FCSTD DOCUMENT  (FreeCAD 0.16R6704 (Git))
Label: Proxxon IBS-E
License: All rights reserved
LicenseURL: http://en.wikipedia.org/wiki/All_rights_reserved
objects: Sketcher::SketchObject×10, Drawing::FeatureViewPython×10, PartDesign::Pocket×9, Drawing::FeatureViewPart×3, Drawing::FeaturePage×2, PartDesign::Fillet×2, Mesh::Feature×1, PartDesign::Pad×1, PartDesign::Chamfer×1
note: 33 computed .brp shape members not serialized (recipe doc carries the construction recipe); baked Part::Feature solids carry a one-line shape summary decoded from their .brp

FEATURE [Mesh::Feature] Proxxon_IBS_E  label="Proxxon_IBS-E"
  Placement = pos=(-33.5,-33.5,0) rot=(0,0,1;0rad)
FEATURE [Sketcher::SketchObject] Sketch
  sketch-geometry (22):
    g0: LineSegment [constr] StartX=-23 StartY=-23.75 StartZ=0 EndX=23 EndY=-23.75 EndZ=0
    g1: LineSegment [constr] StartX=23 StartY=-23.75 StartZ=0 EndX=23 EndY=23.75 EndZ=0
    g2: LineSegment StartX=23 StartY=23.75 StartZ=0 EndX=-23 EndY=23.75 EndZ=0
    g3: LineSegment [constr] StartX=-23 StartY=23.75 StartZ=0 EndX=-23 EndY=-23.75 EndZ=0
    g4: LineSegment StartX=-1 StartY=-23.75 StartZ=0 EndX=-1 EndY=-50.75 EndZ=0
    g5: LineSegment StartX=-1 StartY=-50.75 StartZ=0 EndX=-13 EndY=-50.75 EndZ=0
    g6: LineSegment StartX=-13 StartY=-50.75 StartZ=0 EndX=-13 EndY=-33.75 EndZ=0
    g7: LineSegment StartX=-13 StartY=-33.75 StartZ=0 EndX=-38 EndY=-33.75 EndZ=0
    g8: LineSegment StartX=-38 StartY=-33.75 StartZ=0 EndX=-38 EndY=27.75 EndZ=0
    g9: LineSegment StartX=-38 StartY=27.75 StartZ=0 EndX=38 EndY=27.75 EndZ=0
    g10: LineSegment StartX=38 StartY=27.75 StartZ=0 EndX=38 EndY=-33.75 EndZ=0
    g11: LineSegment StartX=38 StartY=-33.75 StartZ=0 EndX=13 EndY=-33.75 EndZ=0
    g12: LineSegment StartX=13 StartY=-33.75 StartZ=0 EndX=13 EndY=-50.75 EndZ=0
    g13: LineSegment StartX=13 StartY=-50.75 StartZ=0 EndX=1 EndY=-50.75 EndZ=0
    g14: LineSegment StartX=1 StartY=-50.75 StartZ=0 EndX=1 EndY=-23.75 EndZ=0
    g15: LineSegment StartX=-23 StartY=-15.2647 StartZ=0 EndX=-14.5147 EndY=-23.75 EndZ=0
    g16: LineSegment StartX=14.5147 StartY=-23.75 StartZ=0 EndX=23 EndY=-15.2647 EndZ=0
    g17: LineSegment StartX=-14.5147 StartY=-23.75 StartZ=0 EndX=-1 EndY=-23.75 EndZ=0
    g18: LineSegment StartX=1 StartY=-23.75 StartZ=0 EndX=14.5147 EndY=-23.75 EndZ=0
    g19: LineSegment StartX=-23 StartY=23.75 StartZ=0 EndX=-23 EndY=-15.2647 EndZ=0
    g20: LineSegment StartX=23 StartY=23.75 StartZ=0 EndX=23 EndY=-15.2647 EndZ=0
    g21: LineSegment [constr] StartX=-23 StartY=-23.75 StartZ=0 EndX=-18.7574 EndY=-19.5074 EndZ=0
  constraints (65):
    c: Coincident(g0,g1)
    c: Coincident(g1,g2)
    c: Coincident(g2,g3)
    c: Coincident(g3,g0)
    c: Horizontal(g0)
    c: Horizontal(g2)
    c: Vertical(g1)
    c: Vertical(g3)
    c: DistanceY(g3,g3) = 47.5
    c: DistanceX(g2,g2) = 46
    c: Vertical(g4)
    c: Coincident(g4,g5)
    c: Horizontal(g5)
    c: Coincident(g5,g6)
    c: Vertical(g6)
    c: Coincident(g6,g7)
    c: Horizontal(g7)
    c: Coincident(g7,g8)
    c: Vertical(g8)
    c: Coincident(g8,g9)
    c: Horizontal(g9)
    c: Coincident(g9,g10)
    c: Vertical(g10)
    c: Coincident(g10,g11)
    c: Horizontal(g11)
    c: Coincident(g11,g12)
    c: Vertical(g12)
    c: Coincident(g12,g13)
    c: Horizontal(g13)
    c: Coincident(g13,g14)
    c: Vertical(g14)
    c: PointOnObject(g4,g13)
    c: Equal(g13,g5)
    c: Equal(g7,g11)
    c: PointOnObject(g6,g11)
    c: Symmetric(g8,g9,g-2)
    c: DistanceY(g1,g9) = 4
    c: DistanceY(g6,g0) = 10
    c: DistanceX(g5,g5) = 12
    c: DistanceX(g4,g13) = 2
    c: DistanceY(g6,g6) = 17
    c: Symmetric(g2,g1,g-2)
    c: Symmetric(g1,g0,g-1)
    c: DistanceX(g9,g9) = 76
    c: PointOnObject(g15,g3)
    c: PointOnObject(g15,g0)
    c: PointOnObject(g16,g0)
    c: PointOnObject(g16,g1)
    c: Angle(g3,g15) = 0.785398
    c: Angle(g16,g1) = 0.785398
    c: Equal(g15,g16)
    c: Coincident(g15,g17)
    c: Coincident(g4,g17)
    c: Coincident(g14,g18)
    c: Coincident(g16,g18)
    c: Coincident(g15,g19)
    c: Coincident(g2,g19)
    c: Coincident(g1,g20)
    c: Coincident(g16,g20)
    c: Coincident(g21,g0)
    c: PointOnObject(g21,g15)
    c: Distance(g21) = 6
    c: Perpendicular(g15,g21)
    c: PointOnObject(g4,g0)
    c: PointOnObject(g14,g0)
FEATURE [PartDesign::Pad] Pad
  Length = 20
  Length2 = 100
  Sketch = -> Sketch
  Type = 0
FEATURE [Sketcher::SketchObject] Sketch001
  ExternalGeometry = -> [Pad]
  Placement = pos=(-13,0,0) rot=(0.57735,-0.57735,-0.57735;2.0944rad)
  Support = -> Pad [Face7]
  sketch-geometry (3):
    g0: LineSegment [constr] StartX=33.75 StartY=10 StartZ=0 EndX=42.25 EndY=10 EndZ=0
    g1: LineSegment [constr] StartX=42.25 StartY=10 StartZ=0 EndX=50.75 EndY=10 EndZ=0
    g2: Circle CenterX=42.25 CenterY=10 CenterZ=0 NormalX=0 NormalY=0 NormalZ=1 Radius=2.2
  constraints (9):
    c: PointOnObject(g0,g-3)
    c: Horizontal(g0)
    c: Coincident(g0,g1)
    c: PointOnObject(g1,g-4)
    c: Horizontal(g1)
    c: Equal(g0,g1)
    c: Symmetric(g-3,g-3,g0)
    c: Coincident(g2,g0)
    c: Radius(g2) = 2.2
FEATURE [PartDesign::Pocket] Pocket
  Length = 5
  Sketch = -> Sketch001
  Type = 1
FEATURE [Sketcher::SketchObject] Sketch002
  ExternalGeometry = -> [Pocket]
  Placement = pos=(13,0,0) rot=(0.57735,0.57735,0.57735;2.0944rad)
  Support = -> Pocket [Face17]
  sketch-geometry (7):
    g0: LineSegment StartX=-40.2148 StartY=6.475 StartZ=0 EndX=-38.1797 EndY=10 EndZ=0
    g1: LineSegment StartX=-38.1797 StartY=10 StartZ=0 EndX=-40.2148 EndY=13.525 EndZ=0
    g2: LineSegment StartX=-40.2148 StartY=13.525 StartZ=0 EndX=-44.2852 EndY=13.525 EndZ=0
    g3: LineSegment StartX=-44.2852 StartY=13.525 StartZ=0 EndX=-46.3203 EndY=10 EndZ=0
    g4: LineSegment StartX=-46.3203 StartY=10 StartZ=0 EndX=-44.2852 EndY=6.475 EndZ=0
    g5: LineSegment StartX=-44.2852 StartY=6.475 StartZ=0 EndX=-40.2148 EndY=6.475 EndZ=0
    g6: Circle [constr] CenterX=-42.25 CenterY=10 CenterZ=0 NormalX=0 NormalY=0 NormalZ=1 Radius=4.07032
  constraints (16):
    c: Coincident(g0,g1)
    c: Coincident(g1,g2)
    c: Coincident(g2,g3)
    c: Coincident(g3,g4)
    c: Coincident(g4,g5)
    c: Coincident(g5,g0)
    c: Equal(g0, g1-g5) x5
    c: PointOnObject(g0,g6)
    c: PointOnObject(g1,g6)
    c: PointOnObject(g2,g6)
    c: PointOnObject(g3,g6)
    c: PointOnObject(g4,g6)
    c: PointOnObject(g5,g6)
    c: Coincident(g6,g-3)
    c: Distance(g2,g4) = 7.05
    c: Horizontal(g5)
FEATURE [PartDesign::Pocket] Pocket001
  Length = 4
  Sketch = -> Sketch002
  Type = 0
FEATURE [Sketcher::SketchObject] Sketch003
  ExternalGeometry = -> [Pocket001]
  Placement = pos=(0,27.75,0) rot=(0,0.707107,0.707107;3.14159rad)
  Support = -> Pocket001 [Face14]
  sketch-geometry (3):
    g0: LineSegment [constr] StartX=-30 StartY=10 StartZ=0 EndX=30 EndY=10 EndZ=0
    g1: Circle CenterX=-30 CenterY=10 CenterZ=0 NormalX=0 NormalY=0 NormalZ=1 Radius=2.2
    g2: Circle CenterX=30 CenterY=10 CenterZ=0 NormalX=0 NormalY=0 NormalZ=1 Radius=2.2
  constraints (5):
    c: Symmetric(g0,g0,g-2)
    c: Coincident(g1,g0)
    c: Coincident(g2,g0)
    c: Radius(g1) = 2.2
    c: Equal(g1,g2)
FEATURE [PartDesign::Pocket] Pocket002
  Length = 5
  Sketch = -> Sketch003
  Type = 1
FEATURE [Sketcher::SketchObject] Sketch004
  ExternalGeometry = -> [Pocket002]
  Placement = pos=(0,-33.75,0) rot=(1,0,0;1.5708rad)
  Support = -> Pocket002 [Face12]
  sketch-geometry (15):
    g0: LineSegment [constr] StartX=-30 StartY=10 StartZ=0 EndX=30 EndY=10 EndZ=0
    g1: LineSegment StartX=-33.525 StartY=7.96484 StartZ=0 EndX=-30 EndY=5.92968 EndZ=0
    g2: LineSegment StartX=-30 StartY=5.92968 StartZ=0 EndX=-26.475 EndY=7.96484 EndZ=0
    g3: LineSegment StartX=-26.475 StartY=7.96484 StartZ=0 EndX=-26.475 EndY=12.0352 EndZ=0
    g4: LineSegment StartX=-26.475 StartY=12.0352 StartZ=0 EndX=-30 EndY=14.0703 EndZ=0
    g5: LineSegment StartX=-30 StartY=14.0703 StartZ=0 EndX=-33.525 EndY=12.0352 EndZ=0
    g6: LineSegment StartX=-33.525 StartY=12.0352 StartZ=0 EndX=-33.525 EndY=7.96484 EndZ=0
    g7: Circle [constr] CenterX=-30 CenterY=10 CenterZ=0 NormalX=0 NormalY=0 NormalZ=1 Radius=4.07032
    g8: LineSegment StartX=33.525 StartY=7.96484 StartZ=0 EndX=33.525 EndY=12.0352 EndZ=0
    g9: LineSegment StartX=33.525 StartY=12.0352 StartZ=0 EndX=30 EndY=14.0703 EndZ=0
    g10: LineSegment StartX=30 StartY=14.0703 StartZ=0 EndX=26.475 EndY=12.0352 EndZ=0
    g11: LineSegment StartX=26.475 StartY=12.0352 StartZ=0 EndX=26.475 EndY=7.96484 EndZ=0
    g12: LineSegment StartX=26.475 StartY=7.96484 StartZ=0 EndX=30 EndY=5.92968 EndZ=0
    g13: LineSegment StartX=30 StartY=5.92968 StartZ=0 EndX=33.525 EndY=7.96484 EndZ=0
    g14: Circle [constr] CenterX=30 CenterY=10 CenterZ=0 NormalX=0 NormalY=0 NormalZ=1 Radius=4.07032
  constraints (35):
    c: Horizontal(g0)
    c: Symmetric(g0,g0,g-2)
    c: Coincident(g1,g2)
    c: Coincident(g2,g3)
    c: Coincident(g3,g4)
    c: Coincident(g4,g5)
    c: Coincident(g5,g6)
    c: Coincident(g6,g1)
    c: Equal(g1, g2-g6) x5
    c: PointOnObject(g1,g7)
    c: PointOnObject(g2,g7)
    c: PointOnObject(g3,g7)
    c: PointOnObject(g4,g7)
    c: PointOnObject(g5,g7)
    c: PointOnObject(g6,g7)
    c: Coincident(g0,g7)
    c: Distance(g1,g2) = 7.05
    c: Coincident(g8,g9)
    c: Coincident(g9,g10)
    c: Coincident(g10,g11)
    c: Coincident(g11,g12)
    c: Coincident(g12,g13)
    c: Coincident(g13,g8)
    c: Equal(g8, g9-g13) x5
    c: PointOnObject(g8,g14)
    c: PointOnObject(g9,g14)
    c: PointOnObject(g10,g14)
    c: PointOnObject(g11,g14)
    c: PointOnObject(g12,g14)
    c: PointOnObject(g13,g14)
    c: Coincident(g0,g14)
    c: Equal(g7,g14)
    c: Coincident(g0,g-3)
    c: Vertical(g3)
    c: Vertical(g8)
FEATURE [PartDesign::Pocket] Pocket003
  Length = 56.5
  Sketch = -> Sketch004
  Type = 0
FEATURE [Sketcher::SketchObject] Sketch005
  ExternalGeometry = -> [Pocket003]
  Placement = pos=(0,-33.75,0) rot=(1,0,0;1.5708rad)
  Support = -> Pocket003 [Face12]
  sketch-geometry (17):
    g0: LineSegment StartX=30 StartY=15.7735 StartZ=0 EndX=25 EndY=12.8868 EndZ=0
    g1: LineSegment StartX=25 StartY=12.8868 StartZ=0 EndX=25 EndY=7.11325 EndZ=0
    g2: LineSegment StartX=25 StartY=7.11325 StartZ=0 EndX=30 EndY=4.2265 EndZ=0
    g3: LineSegment StartX=30 StartY=4.2265 StartZ=0 EndX=35 EndY=7.11325 EndZ=0
    g4: LineSegment StartX=35 StartY=7.11325 StartZ=0 EndX=35 EndY=12.8868 EndZ=0
    g5: LineSegment StartX=35 StartY=12.8868 StartZ=0 EndX=30 EndY=15.7735 EndZ=0
    g6: Circle [constr] CenterX=30 CenterY=10 CenterZ=0 NormalX=0 NormalY=0 NormalZ=1 Radius=5.7735
    g7: LineSegment StartX=-35 StartY=7.11325 StartZ=0 EndX=-30 EndY=4.2265 EndZ=0
    g8: LineSegment StartX=-30 StartY=4.2265 StartZ=0 EndX=-25 EndY=7.11325 EndZ=0
    g9: LineSegment StartX=-25 StartY=7.11325 StartZ=0 EndX=-25 EndY=12.8868 EndZ=0
    g10: LineSegment StartX=-25 StartY=12.8868 StartZ=0 EndX=-30 EndY=15.7735 EndZ=0
    g11: LineSegment StartX=-30 StartY=15.7735 StartZ=0 EndX=-35 EndY=12.8868 EndZ=0
    g12: LineSegment StartX=-35 StartY=12.8868 StartZ=0 EndX=-35 EndY=7.11325 EndZ=0
    g13: Circle [constr] CenterX=-30 CenterY=10 CenterZ=0 NormalX=0 NormalY=0 NormalZ=1 Radius=5.7735
    g14: LineSegment [constr] StartX=-30 StartY=10 StartZ=0 EndX=30 EndY=10 EndZ=0
    g15: LineSegment [constr] StartX=-30 StartY=14.0703 StartZ=0 EndX=-30 EndY=5.92968 EndZ=0
    g16: LineSegment [constr] StartX=-33.525 StartY=7.96484 StartZ=0 EndX=-26.475 EndY=12.0352 EndZ=0
  constraints (39):
    c: Coincident(g0,g1)
    c: Coincident(g1,g2)
    c: Coincident(g2,g3)
    c: Coincident(g3,g4)
    c: Coincident(g4,g5)
    c: Coincident(g5,g0)
    c: Equal(g0, g1-g5) x5
    c: PointOnObject(g0,g6)
    c: PointOnObject(g1,g6)
    c: PointOnObject(g2,g6)
    c: PointOnObject(g3,g6)
    c: PointOnObject(g4,g6)
    c: PointOnObject(g5,g6)
    c: Coincident(g7,g8)
    c: Coincident(g8,g9)
    c: Coincident(g9,g10)
    c: Coincident(g10,g11)
    c: Coincident(g11,g12)
    c: Coincident(g12,g7)
    c: Equal(g7, g8-g12) x5
    c: PointOnObject(g7,g13)
    c: PointOnObject(g8,g13)
    c: PointOnObject(g9,g13)
    c: PointOnObject(g10,g13)
    c: PointOnObject(g11,g13)
    c: PointOnObject(g12,g13)
    c: Equal(g13,g6)
    c: Distance(g3,g0) = 10
    c: Coincident(g14,g13)
    c: Coincident(g14,g6)
    c: Symmetric(g13,g6,g-2)
    c: PointOnObject(g13,g16)
    c: PointOnObject(g13,g15)
    c: Coincident(g16,g-3)
    c: Coincident(g-3,g15)
    c: Coincident(g-4,g16)
    c: Coincident(g15,g-4)
    c: Vertical(g9)
    c: Vertical(g4)
FEATURE [PartDesign::Pocket] Pocket004
  Length = 51.5
  Sketch = -> Sketch005
  Type = 0
FEATURE [Drawing::FeatureViewPart] Ortho  label="Ortho_0_0"
  Direction = (0,0,1)
  HiddenWidth = 0.15
  LineWidth = 0.35
  Rotation = 0
  ShowHiddenLines = false
  ShowSmoothLines = false
  Tolerance = 0.05
  ViewResult = <blob: 2354 chars omitted>
  Visible = true
  X = 112.333
  Y = 74.5
FEATURE [Drawing::FeatureViewPart] Ortho001  label="Ortho_1_0"
  Direction = (1,0,0)
  HiddenWidth = 0.15
  LineWidth = 0.35
  Rotation = 180
  ShowHiddenLines = false
  ShowSmoothLines = false
  Tolerance = 0.05
  ViewResult = <blob: 3490 chars omitted>
  Visible = true
  X = 239.667
  Y = 74.5
FEATURE [Drawing::FeatureViewPython] dim001  # drawing view (typed FeaturePython)
  Rotation = 0
  ViewResult = <g> \n  <line x1="135.583000" y1="48.750000" x2="135.583000" y2="25.299539" style="stroke:rgb(0,0,255);stroke-width:0.30" />\n<line x1="89.083000" y1="48.750000" x2="89.083000" y2="25.299539" style="stroke:rgb(0,0,255);stroke-width:0.30" />\n<line x1="135.583000" y1="26.299539" x2="89.083000" y2="26.299539" style="stroke:rgb(0,0,255);stroke-width:0.30" /> \n  <polygon points="89.083000,26.299539 92.083000,27.299539 93.083000,26.299539 92.083000,25.299539" style="fill:rgb(0,0,255);stroke:rgb(0,0,255);stroke-width:0" /><polygon points="135.583000,26.299539 132.583000,25.299539 131.583000,26.299539 132.583000,27.299539" style="fill:rgb(0,0,255);stroke:rgb(0,0,255);stroke-width:0" /> \n  <text x="112.333000" y="24.299539" font-family="Verdana" font-size="3.6" fill="rgb(0,0,255)" text-anchor="middle" transform="rotate(0.000000 112.333000,24.299539)" >46.5</text> </g>
  Visible = true
  X = 0
  Y = 0
  arrowL1 = 3
  arrowL2 = 1
  arrowW = 2
  arrow_scheme = 0
  autoPlaceOffset = 2
  autoPlaceText = true
  click1_x = 98.8424
  click1_y = 26.2995
  click2_x = 98.8424
  click2_y = 26.2995
  comma_decimal_place = false
  dimension_line_overshoot = 1
  gap_datum_points = 2
  halfDimension_linear = false
  lineColor = rgb(0,0,255)
  strokeWidth = 0.3
  textFormat_linear = %(value)3.3f
  textRenderer_color = rgb(0,0,255)
  textRenderer_family = Verdana
  textRenderer_size = 3.6
  unit_custom_scale = 1
  unit_scheme = 0
FEATURE [Drawing::FeatureViewPython] dim002  # drawing view (typed FeaturePython)
  Rotation = 0
  ViewResult = <g> \n  <line x1="87.083000" y1="50.750000" x2="39.764285" y2="50.750000" style="stroke:rgb(0,0,255);stroke-width:0.30" />\n<line x1="87.083000" y1="98.250000" x2="39.764285" y2="98.250000" style="stroke:rgb(0,0,255);stroke-width:0.30" />\n<line x1="40.764285" y1="50.750000" x2="40.764285" y2="98.250000" style="stroke:rgb(0,0,255);stroke-width:0.30" /> \n  <polygon points="40.764285,98.250000 41.764285,95.250000 40.764285,94.250000 39.764285,95.250000" style="fill:rgb(0,0,255);stroke:rgb(0,0,255);stroke-width:0" /><polygon points="40.764285,50.750000 39.764285,53.750000 40.764285,54.750000 41.764285,53.750000" style="fill:rgb(0,0,255);stroke:rgb(0,0,255);stroke-width:0" /> \n  <text x="38.764285" y="74.500000" font-family="Verdana" font-size="3.6" fill="rgb(0,0,255)" text-anchor="middle" transform="rotate(-90.000000 38.764285,74.500000)" >47.5</text> </g>
  Visible = true
  X = 0
  Y = 0
  arrowL1 = 3
  arrowL2 = 1
  arrowW = 2
  arrow_scheme = 0
  autoPlaceOffset = 2
  autoPlaceText = true
  click1_x = 40.7643
  click1_y = 68.3788
  click2_x = 40.7643
  click2_y = 68.3788
  comma_decimal_place = false
  dimension_line_overshoot = 1
  gap_datum_points = 2
  halfDimension_linear = false
  lineColor = rgb(0,0,255)
  strokeWidth = 0.3
  textFormat_linear = %(value)3.3f
  textRenderer_color = rgb(0,0,255)
  textRenderer_family = Verdana
  textRenderer_size = 3.6
  unit_custom_scale = 1
  unit_scheme = 0
FEATURE [Drawing::FeatureViewPython] dim003  # drawing view (typed FeaturePython)
  Rotation = 0
  ViewResult = <g> \n  <line x1="154.333000" y1="46.750000" x2="176.549420" y2="46.750000" style="stroke:rgb(0,0,255);stroke-width:0.30" />\n<line x1="151.333000" y1="108.250000" x2="176.549420" y2="108.250000" style="stroke:rgb(0,0,255);stroke-width:0.30" />\n<line x1="175.549420" y1="46.750000" x2="175.549420" y2="108.250000" style="stroke:rgb(0,0,255);stroke-width:0.30" /> \n  <polygon points="175.549420,108.250000 176.549420,105.250000 175.549420,104.250000 174.549420,105.250000" style="fill:rgb(0,0,255);stroke:rgb(0,0,255);stroke-width:0" /><polygon points="175.549420,46.750000 174.549420,49.750000 175.549420,50.750000 176.549420,49.750000" style="fill:rgb(0,0,255);stroke:rgb(0,0,255);stroke-width:0" /> \n  <text x="173.549420" y="77.500000" font-family="Verdana" font-size="3.6" fill="rgb(0,0,255)" text-anchor="middle" transform="rotate(-90.000000 173.549420,77.500000)" >61.5</text> </g>
  Visible = true
  X = 0
  Y = 0
  arrowL1 = 3
  arrowL2 = 1
  arrowW = 2
  arrow_scheme = 0
  autoPlaceOffset = 2
  autoPlaceText = true
  click1_x = 175.549
  click1_y = 87.446
  click2_x = 175.549
  click2_y = 87.446
  comma_decimal_place = false
  dimension_line_overshoot = 1
  gap_datum_points = 2
  halfDimension_linear = false
  lineColor = rgb(0,0,255)
  strokeWidth = 0.3
  textFormat_linear = %(value)3.3f
  textRenderer_color = rgb(0,0,255)
  textRenderer_family = Verdana
  textRenderer_size = 3.6
  unit_custom_scale = 1
  unit_scheme = 0
FEATURE [Drawing::FeatureViewPython] dim004  # drawing view (typed FeaturePython)
  Rotation = 0
  ViewResult = <g> \n  <line x1="72.333000" y1="44.750000" x2="72.333000" y2="17.848003" style="stroke:rgb(0,0,255);stroke-width:0.30" />\n<line x1="152.333000" y1="44.750000" x2="152.333000" y2="17.848003" style="stroke:rgb(0,0,255);stroke-width:0.30" />\n<line x1="72.333000" y1="18.848003" x2="152.333000" y2="18.848003" style="stroke:rgb(0,0,255);stroke-width:0.30" /> \n  <polygon points="152.333000,18.848003 149.333000,17.848003 148.333000,18.848003 149.333000,19.848003" style="fill:rgb(0,0,255);stroke:rgb(0,0,255);stroke-width:0" /><polygon points="72.333000,18.848003 75.333000,19.848003 76.333000,18.848003 75.333000,17.848003" style="fill:rgb(0,0,255);stroke:rgb(0,0,255);stroke-width:0" /> \n  <text x="112.333000" y="16.848003" font-family="Verdana" font-size="3.6" fill="rgb(0,0,255)" text-anchor="middle" transform="rotate(0.000000 112.333000,16.848003)" >80</text> </g>
  Visible = true
  X = 0
  Y = 0
  arrowL1 = 3
  arrowL2 = 1
  arrowW = 2
  arrow_scheme = 0
  autoPlaceOffset = 2
  autoPlaceText = true
  click1_x = 146.182
  click1_y = 18.848
  click2_x = 146.182
  click2_y = 18.848
  comma_decimal_place = false
  dimension_line_overshoot = 1
  gap_datum_points = 2
  halfDimension_linear = false
  lineColor = rgb(0,0,255)
  strokeWidth = 0.3
  textFormat_linear = %(value)3.3f
  textRenderer_color = rgb(0,0,255)
  textRenderer_family = Verdana
  textRenderer_size = 3.6
  unit_custom_scale = 1
  unit_scheme = 0
FEATURE [Drawing::FeatureViewPython] dim005  # drawing view (typed FeaturePython)
  Rotation = 0
  ViewResult = <g> \n  <line x1="219.667000" y1="44.750000" x2="219.667000" y2="31.655260" style="stroke:rgb(0,0,255);stroke-width:0.30" />\n<line x1="239.667000" y1="44.750000" x2="239.667000" y2="31.655260" style="stroke:rgb(0,0,255);stroke-width:0.30" />\n<line x1="219.667000" y1="32.655260" x2="239.667000" y2="32.655260" style="stroke:rgb(0,0,255);stroke-width:0.30" /> \n  <polygon points="239.667000,32.655260 236.667000,31.655260 235.667000,32.655260 236.667000,33.655260" style="fill:rgb(0,0,255);stroke:rgb(0,0,255);stroke-width:0" /><polygon points="219.667000,32.655260 222.667000,33.655260 223.667000,32.655260 222.667000,31.655260" style="fill:rgb(0,0,255);stroke:rgb(0,0,255);stroke-width:0" /> \n  <text x="229.667000" y="30.655260" font-family="Verdana" font-size="3.6" fill="rgb(0,0,255)" text-anchor="middle" transform="rotate(0.000000 229.667000,30.655260)" >20</text> </g>
  Visible = true
  X = 0
  Y = 0
  arrowL1 = 3
  arrowL2 = 1
  arrowW = 2
  arrow_scheme = 0
  autoPlaceOffset = 2
  autoPlaceText = true
  click1_x = 239.107
  click1_y = 32.6553
  click2_x = 239.107
  click2_y = 32.6553
  comma_decimal_place = false
  dimension_line_overshoot = 1
  gap_datum_points = 2
  halfDimension_linear = false
  lineColor = rgb(0,0,255)
  strokeWidth = 0.3
  textFormat_linear = %(value)3.3f
  textRenderer_color = rgb(0,0,255)
  textRenderer_family = Verdana
  textRenderer_size = 3.6
  unit_custom_scale = 1
  unit_scheme = 0
FEATURE [Drawing::FeaturePage] Page
  EditableTexts = AUTHOR NAME | DRAWING TITLE | FreeCAD DRAWING | A4 | X / Y | SCALE | PN | DN | DD/MM/YYYY | REV A
  Group = -> [Ortho,Ortho001,dim001,dim002,dim003,dim004,dim005]
FEATURE [Sketcher::SketchObject] Sketch006
  ExternalGeometry = -> [Pocket004]
  Placement = pos=(-19.1324,-19.1324,0) rot=(0.281085,0.678598,0.678598;2.59356rad)
  Support = -> Pocket004 [Face7]
  sketch-geometry (10):
    g0: LineSegment [constr] StartX=-0.53033 StartY=5.92968 StartZ=0 EndX=2.99467 EndY=7.96484 EndZ=0
    g1: LineSegment [constr] StartX=2.99467 StartY=7.96484 StartZ=0 EndX=2.99467 EndY=12.0352 EndZ=0
    g2: LineSegment [constr] StartX=2.99467 StartY=12.0352 StartZ=0 EndX=-0.53033 EndY=14.0703 EndZ=0
    g3: LineSegment [constr] StartX=-0.53033 StartY=14.0703 StartZ=0 EndX=-4.05533 EndY=12.0352 EndZ=0
    g4: LineSegment [constr] StartX=-4.05533 StartY=12.0352 StartZ=0 EndX=-4.05533 EndY=7.96484 EndZ=0
    g5: LineSegment [constr] StartX=-4.05533 StartY=7.96484 StartZ=0 EndX=-0.53033 EndY=5.92968 EndZ=0
    g6: Circle [constr] CenterX=-0.53033 CenterY=10 CenterZ=0 NormalX=0 NormalY=0 NormalZ=1 Radius=4.07032
    g7: LineSegment [constr] StartX=5.46967 StartY=20 StartZ=0 EndX=-6.53033 EndY=0 EndZ=0
    g8: Circle CenterX=-0.53033 CenterY=10 CenterZ=0 NormalX=0 NormalY=0 NormalZ=1 Radius=1.7
    g9: LineSegment [constr] StartX=-6.53033 StartY=20 StartZ=0 EndX=5.46967 EndY=0 EndZ=0
  constraints (23):
    c: Coincident(g0,g1)
    c: Coincident(g1,g2)
    c: Coincident(g2,g3)
    c: Coincident(g3,g4)
    c: Coincident(g4,g5)
    c: Coincident(g5,g0)
    c: Equal(g0, g1-g5) x5
    c: PointOnObject(g0,g6)
    c: PointOnObject(g1,g6)
    c: PointOnObject(g2,g6)
    c: PointOnObject(g3,g6)
    c: PointOnObject(g4,g6)
    c: PointOnObject(g5,g6)
    c: Distance(g4,g0) = 7.05
    c: Vertical(g1)
    c: Coincident(g7,g-3)
    c: PointOnObject(g6,g7)
    c: Coincident(g8,g6)
    c: Radius(g8) = 1.7
    c: Coincident(g9,g-3)
    c: Coincident(g9,g-4)
    c: PointOnObject(g6,g9)
    c: Coincident(g7,g-4)
FEATURE [PartDesign::Pocket] Pocket005
  Length = 5
  Sketch = -> Sketch006
  Type = 1
FEATURE [Sketcher::SketchObject] Sketch007
  ExternalGeometry = -> [Pocket005]
  Placement = pos=(-19.1324,-19.1324,0) rot=(0.281085,0.678598,0.678598;2.59356rad)
  Support = -> Pocket005 [Face7]
  sketch-geometry (7):
    g0: LineSegment StartX=-0.53033 StartY=6.79571 StartZ=0 EndX=2.24467 EndY=8.39785 EndZ=0
    g1: LineSegment StartX=2.24467 StartY=8.39785 StartZ=0 EndX=2.24467 EndY=11.6021 EndZ=0
    g2: LineSegment StartX=2.24467 StartY=11.6021 StartZ=0 EndX=-0.53033 EndY=13.2043 EndZ=0
    g3: LineSegment StartX=-0.53033 StartY=13.2043 StartZ=0 EndX=-3.30533 EndY=11.6021 EndZ=0
    g4: LineSegment StartX=-3.30533 StartY=11.6021 StartZ=0 EndX=-3.30533 EndY=8.39785 EndZ=0
    g5: LineSegment StartX=-3.30533 StartY=8.39785 StartZ=0 EndX=-0.53033 EndY=6.79571 EndZ=0
    g6: Circle [constr] CenterX=-0.53033 CenterY=10 CenterZ=0 NormalX=0 NormalY=0 NormalZ=1 Radius=3.20429
  constraints (16):
    c: Coincident(g0,g1)
    c: Coincident(g1,g2)
    c: Coincident(g2,g3)
    c: Coincident(g3,g4)
    c: Coincident(g4,g5)
    c: Coincident(g5,g0)
    c: Equal(g0, g1-g5) x5
    c: PointOnObject(g0,g6)
    c: PointOnObject(g1,g6)
    c: PointOnObject(g2,g6)
    c: PointOnObject(g3,g6)
    c: PointOnObject(g4,g6)
    c: PointOnObject(g5,g6)
    c: Distance(g0,g1) = 5.55
    c: Coincident(g6,g-3)
    c: Vertical(g1)
FEATURE [PartDesign::Pocket] Pocket006
  Length = 3
  Sketch = -> Sketch007
  Type = 0
FEATURE [Sketcher::SketchObject] Sketch008
  ExternalGeometry = -> [Pocket006]
  Placement = pos=(19.1324,-19.1324,0) rot=(-0.281085,0.678598,0.678598;3.68962rad)
  Support = -> Pocket006 [Face6]
  sketch-geometry (3):
    g0: LineSegment [constr] StartX=-5.46967 StartY=0 StartZ=0 EndX=6.53033 EndY=20 EndZ=0
    g1: LineSegment [constr] StartX=6.53033 StartY=0 StartZ=0 EndX=-5.46967 EndY=20 EndZ=0
    g2: Circle CenterX=0.53033 CenterY=10 CenterZ=0 NormalX=0 NormalY=0 NormalZ=1 Radius=1.7
  constraints (7):
    c: Coincident(g0,g-4)
    c: Coincident(g0,g-3)
    c: Coincident(g1,g-4)
    c: Coincident(g1,g-3)
    c: PointOnObject(g2,g0)
    c: PointOnObject(g2,g1)
    c: Radius(g2) = 1.7
FEATURE [PartDesign::Pocket] Pocket007
  Length = 5
  Sketch = -> Sketch008
  Type = 1
FEATURE [Sketcher::SketchObject] Sketch009
  ExternalGeometry = -> [Pocket007]
  Placement = pos=(19.1324,-19.1324,0) rot=(-0.281085,0.678598,0.678598;3.68962rad)
  Support = -> Pocket007 [Face6]
  sketch-geometry (7):
    g0: LineSegment StartX=3.30533 StartY=8.39785 StartZ=0 EndX=3.30533 EndY=11.6021 EndZ=0
    g1: LineSegment StartX=3.30533 StartY=11.6021 StartZ=0 EndX=0.53033 EndY=13.2043 EndZ=0
    g2: LineSegment StartX=0.53033 StartY=13.2043 StartZ=0 EndX=-2.24467 EndY=11.6021 EndZ=0
    g3: LineSegment StartX=-2.24467 StartY=11.6021 StartZ=0 EndX=-2.24467 EndY=8.39785 EndZ=0
    g4: LineSegment StartX=-2.24467 StartY=8.39785 StartZ=0 EndX=0.53033 EndY=6.79571 EndZ=0
    g5: LineSegment StartX=0.53033 StartY=6.79571 StartZ=0 EndX=3.30533 EndY=8.39785 EndZ=0
    g6: Circle [constr] CenterX=0.53033 CenterY=10 CenterZ=0 NormalX=0 NormalY=0 NormalZ=1 Radius=3.20429
  constraints (16):
    c: Coincident(g0,g1)
    c: Coincident(g1,g2)
    c: Coincident(g2,g3)
    c: Coincident(g3,g4)
    c: Coincident(g4,g5)
    c: Coincident(g5,g0)
    c: Equal(g0, g1-g5) x5
    c: PointOnObject(g0,g6)
    c: PointOnObject(g1,g6)
    c: PointOnObject(g2,g6)
    c: PointOnObject(g3,g6)
    c: PointOnObject(g4,g6)
    c: PointOnObject(g5,g6)
    c: Vertical(g0)
    c: Coincident(g6,g-3)
    c: Distance(g3,g0) = 5.55
FEATURE [PartDesign::Pocket] Pocket008
  Length = 2.5
  Sketch = -> Sketch009
  Type = 0
FEATURE [PartDesign::Fillet] Fillet
  Base = -> Pocket008 [Edge2,Edge1]
  Radius = 10
FEATURE [Drawing::FeatureViewPython] dim007  # drawing view (typed FeaturePython)
  Rotation = 0
  ViewResult = <g> \n  <line x1="242.176026" y1="139.853454" x2="233.191797" y2="148.838191" style="stroke:rgb(0,0,255);stroke-width:0.30" />\n<line x1="245.711626" y1="143.388854" x2="236.727397" y2="152.373591" style="stroke:rgb(0,0,255);stroke-width:0.30" />\n<line x1="233.898884" y1="148.131064" x2="237.434484" y2="151.666464" style="stroke:rgb(0,0,255);stroke-width:0.30" /> \n  <polygon points="237.434484,151.666464 238.848778,154.494851 240.262991,154.494811 240.262951,153.080598" style="fill:rgb(0,0,255);stroke:rgb(0,0,255);stroke-width:0" /><polygon points="233.898884,148.131064 232.484591,145.302677 231.070377,145.302717 231.070417,146.716930" style="fill:rgb(0,0,255);stroke:rgb(0,0,255);stroke-width:0" /> \n  <text x="234.252431" y="148.484590" font-family="Verdana" font-size="3.6" fill="rgb(0,0,255)" text-anchor="middle" transform="rotate(-45.001621 234.252431,148.484590)" >2.5</text> </g>
  Visible = true
  X = 0
  Y = 0
  arrowL1 = 3
  arrowL2 = 1
  arrowW = 2
  arrow_scheme = 0
  autoPlaceOffset = 2
  autoPlaceText = true
  click1_x = 236.949
  click1_y = 151.181
  click2_x = 236.949
  click2_y = 151.181
  comma_decimal_place = false
  dimension_line_overshoot = 1
  gap_datum_points = 2
  halfDimension_linear = false
  lineColor = rgb(0,0,255)
  strokeWidth = 0.3
  textFormat_linear = %(value)3.3f
  textRenderer_color = rgb(0,0,255)
  textRenderer_family = Verdana
  textRenderer_size = 3.6
  unit_custom_scale = 1
  unit_scheme = 0
FEATURE [PartDesign::Fillet] Fillet001
  Base = -> Fillet [Edge45,Edge47,Edge54,Edge46,Edge87,Edge76,Edge68,Edge67,Edge78,Edge69]
  Radius = 2.5
FEATURE [PartDesign::Chamfer] Chamfer
  Base = -> Fillet001 [Edge30,Edge130,Edge116,Edge105,Edge72,Edge86,Edge103,Edge18,Edge14,Edge23,Edge22,Edge27]
  Size = 2
FEATURE [Drawing::FeatureViewPart] Ortho002  label="Ortho_0_001"
  Direction = (0,0,1)
  HiddenWidth = 0.15
  LineWidth = 0.35
  Rotation = 0
  Scale = 2
  ShowHiddenLines = true
  ShowSmoothLines = false
  Source = -> Chamfer
  Tolerance = 0.05
  ViewResult = <blob: 19424 chars omitted>
  Visible = true
  X = 210
  Y = 95.5
FEATURE [Drawing::FeatureViewPython] dim006  # drawing view (typed FeaturePython)
  Rotation = 0
  ViewResult = <g> \n  <line x1="262.914214" y1="142.277386" x2="287.656902" y2="117.534698" style="stroke:rgb(0,0,255);stroke-width:0.30" />\n<line x1="254.868614" y1="134.231786" x2="279.611302" y2="109.489098" style="stroke:rgb(0,0,255);stroke-width:0.30" />\n<line x1="286.949795" y1="118.241805" x2="278.904195" y2="110.196205" style="stroke:rgb(0,0,255);stroke-width:0.30" /> \n  <polygon points="278.904195,110.196205 280.318408,113.024632 281.732622,113.024632 281.732622,111.610419" style="fill:rgb(0,0,255);stroke:rgb(0,0,255);stroke-width:0" /><polygon points="286.949795,118.241805 285.535581,115.413378 284.121368,115.413378 284.121368,116.827592" style="fill:rgb(0,0,255);stroke:rgb(0,0,255);stroke-width:0" /> \n  <text x="281.512781" y="112.804792" font-family="Verdana" font-size="3.6" fill="rgb(0,0,255)" text-anchor="middle" transform="rotate(-45.000000 281.512781,112.804792)" >5.689</text> </g>
  Visible = true
  X = 0
  Y = 0
  arrowL1 = 3
  arrowL2 = 1
  arrowW = 2
  arrow_scheme = 0
  autoPlaceOffset = 2
  autoPlaceText = true
  click1_x = 285.492
  click1_y = 116.784
  click2_x = 285.492
  click2_y = 116.784
  comma_decimal_place = false
  dimension_line_overshoot = 1
  gap_datum_points = 2
  halfDimension_linear = false
  lineColor = rgb(0,0,255)
  strokeWidth = 0.3
  textFormat_linear = %(value)3.3f
  textRenderer_color = rgb(0,0,255)
  textRenderer_family = Verdana
  textRenderer_size = 3.6
  unit_custom_scale = 1
  unit_scheme = 0
FEATURE [Drawing::FeatureViewPython] dim008  # drawing view (typed FeaturePython)
  Rotation = 0
  ViewResult = <g> \n  <line x1="256.000000" y1="120.715800" x2="256.000000" y2="109.316077" style="stroke:rgb(0,0,255);stroke-width:0.30" />\n<line x1="261.500000" y1="161.000000" x2="261.500000" y2="109.316077" style="stroke:rgb(0,0,255);stroke-width:0.30" />\n<line x1="256.000000" y1="110.316077" x2="261.500000" y2="110.316077" style="stroke:rgb(0,0,255);stroke-width:0.30" /> \n  <polygon points="261.500000,110.316077 264.500000,111.316077 265.500000,110.316077 264.500000,109.316077" style="fill:rgb(0,0,255);stroke:rgb(0,0,255);stroke-width:0" /><polygon points="256.000000,110.316077 253.000000,109.316077 252.000000,110.316077 253.000000,111.316077" style="fill:rgb(0,0,255);stroke:rgb(0,0,255);stroke-width:0" /> \n  <text x="258.750000" y="108.316077" font-family="Verdana" font-size="3.6" fill="rgb(0,0,255)" text-anchor="middle" transform="rotate(0.000000 258.750000,108.316077)" >2.75</text> </g>
  Visible = true
  X = 0
  Y = 0
  arrowL1 = 3
  arrowL2 = 1
  arrowW = 2
  arrow_scheme = 0
  autoPlaceOffset = 2
  autoPlaceText = true
  click1_x = 261.078
  click1_y = 110.316
  click2_x = 261.078
  click2_y = 110.316
  comma_decimal_place = false
  dimension_line_overshoot = 1
  gap_datum_points = 2
  halfDimension_linear = false
  lineColor = rgb(0,0,255)
  strokeWidth = 0.3
  textFormat_linear = %(value)3.3f
  textRenderer_color = rgb(0,0,255)
  textRenderer_family = Verdana
  textRenderer_size = 3.6
  unit_custom_scale = 1
  unit_scheme = 0
FEATURE [Drawing::FeatureViewPython] dim009  # drawing view (typed FeaturePython)
  Rotation = 0
  ViewResult = <g> \n  <line x1="260.000000" y1="165.000000" x2="260.000000" y2="167.146258" style="stroke:rgb(0,0,255);stroke-width:0.30" />\n<line x1="256.000000" y1="124.715800" x2="256.000000" y2="167.146258" style="stroke:rgb(0,0,255);stroke-width:0.30" />\n<line x1="260.000000" y1="166.146258" x2="256.000000" y2="166.146258" style="stroke:rgb(0,0,255);stroke-width:0.30" /> \n  <polygon points="256.000000,166.146258 253.000000,165.146258 252.000000,166.146258 253.000000,167.146258" style="fill:rgb(0,0,255);stroke:rgb(0,0,255);stroke-width:0" /><polygon points="260.000000,166.146258 263.000000,167.146258 264.000000,166.146258 263.000000,165.146258" style="fill:rgb(0,0,255);stroke:rgb(0,0,255);stroke-width:0" /> \n  <text x="258.000000" y="164.146258" font-family="Verdana" font-size="3.6" fill="rgb(0,0,255)" text-anchor="middle" transform="rotate(0.000000 258.000000,164.146258)" >2</text> </g>
  Visible = true
  X = 0
  Y = 0
  arrowL1 = 3
  arrowL2 = 1
  arrowW = 2
  arrow_scheme = 0
  autoPlaceOffset = 2
  autoPlaceText = true
  click1_x = 258.762
  click1_y = 166.146
  click2_x = 258.762
  click2_y = 166.146
  comma_decimal_place = false
  dimension_line_overshoot = 1
  gap_datum_points = 2
  halfDimension_linear = false
  lineColor = rgb(0,0,255)
  strokeWidth = 0.3
  textFormat_linear = %(value)3.3f
  textRenderer_color = rgb(0,0,255)
  textRenderer_family = Verdana
  textRenderer_size = 3.6
  unit_custom_scale = 1
  unit_scheme = 0
FEATURE [Drawing::FeatureViewPython] dim010  # drawing view (typed FeaturePython)
  Rotation = 0
  ViewResult = <g> \n  <line x1="143.600000" y1="40.000000" x2="125.411008" y2="40.000000" style="stroke:rgb(0,0,255);stroke-width:0.30" />\n<line x1="143.600000" y1="50.000000" x2="125.411008" y2="50.000000" style="stroke:rgb(0,0,255);stroke-width:0.30" />\n<line x1="126.411008" y1="40.000000" x2="126.411008" y2="50.000000" style="stroke:rgb(0,0,255);stroke-width:0.30" /> \n  <polygon points="126.411008,50.000000 125.411008,53.000000 126.411008,54.000000 127.411008,53.000000" style="fill:rgb(0,0,255);stroke:rgb(0,0,255);stroke-width:0" /><polygon points="126.411008,40.000000 127.411008,37.000000 126.411008,36.000000 125.411008,37.000000" style="fill:rgb(0,0,255);stroke:rgb(0,0,255);stroke-width:0" /> \n  <text x="124.411008" y="45.000000" font-family="Verdana" font-size="3.6" fill="rgb(0,0,255)" text-anchor="middle" transform="rotate(-90.000000 124.411008,45.000000)" >5</text> </g>
  Visible = true
  X = 0
  Y = 0
  arrowL1 = 3
  arrowL2 = 1
  arrowW = 2
  arrow_scheme = 0
  autoPlaceOffset = 2
  autoPlaceText = true
  click1_x = 126.411
  click1_y = 43.969
  click2_x = 126.411
  click2_y = 43.969
  comma_decimal_place = false
  dimension_line_overshoot = 1
  gap_datum_points = 2
  halfDimension_linear = false
  lineColor = rgb(0,0,255)
  strokeWidth = 0.3
  textFormat_linear = %(value)3.3f
  textRenderer_color = rgb(0,0,255)
  textRenderer_family = Verdana
  textRenderer_size = 3.6
  unit_custom_scale = 1
  unit_scheme = 0
FEATURE [Drawing::FeaturePage] Page001
  EditableTexts = AUTHOR NAME | CREATION DATE | SUPERVISOR NAME | CHECK DATE | SCALE | WEIGHT | NUMBER | SHEET | TITLE | SUBTITLE
  Group = -> [Ortho002,dim007,dim006,dim008,dim009,dim010]
